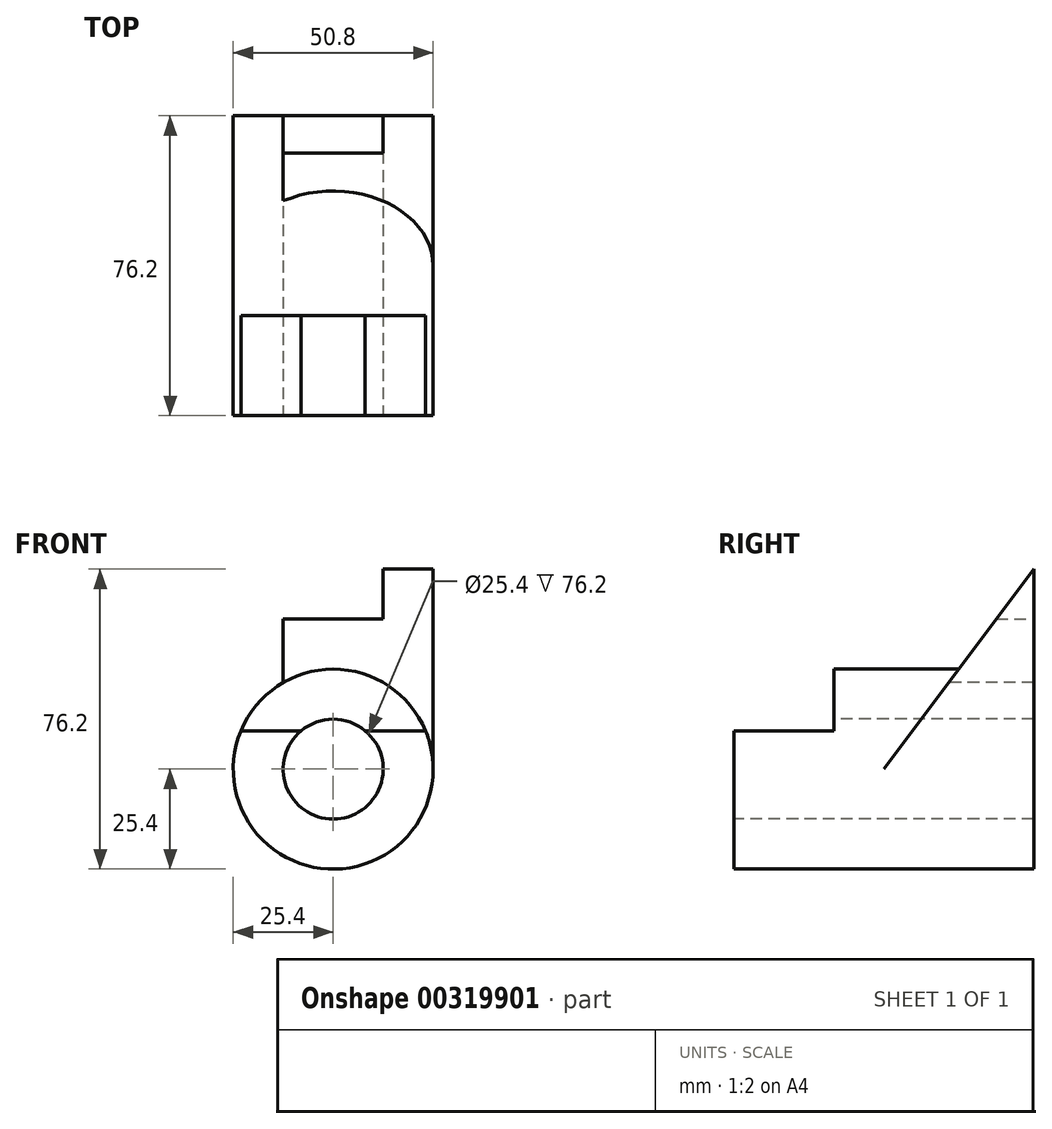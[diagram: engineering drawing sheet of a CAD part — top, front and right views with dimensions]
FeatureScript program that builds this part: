
annotation { "Feature Type Name" : "Feature", "Feature Type Description" : "" }
export const myFeature = defineFeature(function(context is Context, id is Id, definition is map)
    precondition{}
    {
        {
            var Q0;
            Q0=qCreatedBy(makeId("Front.planeOp"),FACE);
            var sketch = newSketch(context, id + "F0", { "sketchPlane" : qUnion([Q0])});
            skCircle(sketch, "E0", {"center": v(0, 0) * mm, "radius": 12.7 * mm});
            skCircle(sketch, "E1", {"center": v(0, 0) * mm, "radius": 25.4 * mm});
            skSolve(sketch);
        }
        {
            var Q0;
            Q0=makeQuery(id+"F0.imprint","IMPRINT",FACE,{"disambiguationData":[TD([[makeQuery(id+"F0.imprint","IMPRINT",EDGE,{"derivedFrom":sQuery(id+"F0.wireOp",EDGE,"E0")}),-1.0]])]});
            extrude(context, id + "F1", {"entities" : qUnion([Q0]), "oppositeDirection" : true, "depth" : 76.2 * mm});
        }
        {
            var Q0;
            Q0=makeQuery(id+"F1.opExtrude","CAP_FACE",FACE,{"disambiguationData":[OSD([sQuery(id+"F0.wireOp",EDGE,"E0"),sQuery(id+"F0.wireOp",EDGE,"E1")])],"isStart":true});
            var sketch = newSketch(context, id + "F2", { "sketchPlane" : qUnion([Q0])});
            skLineSegment(sketch, "E2", {"start": v(0, 25.4) * mm, "end": v(0, 9.53) * mm, "construction": true});
            skLineSegment(sketch, "E3.bottom", {"start": v(25.4, 9.75) * mm, "end": v(-25.4, 9.75) * mm});
            skLineSegment(sketch, "E3.top", {"start": v(25.4, 41.05) * mm, "end": v(-25.4, 41.05) * mm});
            skLineSegment(sketch, "E3.left", {"start": v(25.4, 9.75) * mm, "end": v(25.4, 41.05) * mm});
            skLineSegment(sketch, "E3.right", {"start": v(-25.4, 9.75) * mm, "end": v(-25.4, 41.05) * mm});
            skPoint(sketch, "E3.middle", {"position": v(0, 25.4) * mm});
            skSolve(sketch);
        }
        {
            var Q0;
            {var subQ0=sQuery(id+"F2.wireOp",EDGE,"E3.bottom");var subQ1=makeQuery(id+"F1.opExtrude","CAP_EDGE",EDGE,{"disambiguationData":[OSD([sQuery(id+"F0.wireOp",EDGE,"E1")])],"isStart":true});var subQ2=makeQuery(id+"F2.imprint","INTERSECT",VERTEX,{"disambiguationData":[OD(0.0)],"derivedFrom":[subQ1,subQ0]});Q0=makeQuery(id+"F2.imprint","IMPRINT",FACE,{"disambiguationData":[TD([[makeQuery(id+"F2.imprint","IMPRINT",EDGE,{"disambiguationData":[TD([[subQ2,-1.0]])],"derivedFrom":subQ0}),-1.0]])]});}
            extrude(context, id + "F3", {"entities" : qUnion([Q0]), "operationType" : NewBodyOperationType.REMOVE, "oppositeDirection" : true, "depth" : 12.7 * mm});
        }
        {
            var Q0;
            Q0=makeQuery(id+"F1.opExtrude","CAP_FACE",FACE,{"disambiguationData":[OSD([sQuery(id+"F0.wireOp",EDGE,"E0"),sQuery(id+"F0.wireOp",EDGE,"E1")])],"isStart":true});
            var sketch = newSketch(context, id + "F4", { "sketchPlane" : qUnion([Q0])});
            skPoint(sketch, "E4.endSnap0", {"position": v(0, -12.7) * mm});
            skLineSegment(sketch, "E5", {"start": v(0, 0) * mm, "end": v(0, -9.53) * mm, "construction": true});
            skLineSegment(sketch, "E6", {"start": v(0, -9.53) * mm, "end": v(0, 7.94) * mm, "construction": true});
            skLineSegment(sketch, "E7.bottom", {"start": v(38.1, -9.52) * mm, "end": v(-38.1, -9.53) * mm});
            skLineSegment(sketch, "E7.top", {"start": v(38.1, 25.4) * mm, "end": v(-38.1, 25.4) * mm});
            skLineSegment(sketch, "E7.left", {"start": v(38.1, -9.52) * mm, "end": v(38.1, 25.4) * mm});
            skLineSegment(sketch, "E7.right", {"start": v(-38.1, -9.53) * mm, "end": v(-38.1, 25.4) * mm});
            skPoint(sketch, "E7.middle", {"position": v(0, 7.94) * mm});
            skSolve(sketch);
        }
        {
            var Q0;
            Q0=makeQuery(id+"F4.imprint","IMPRINT",FACE,{"disambiguationData":[TD([[makeQuery(id+"F4.imprint","IMPRINT",EDGE,{"derivedFrom":sQuery(id+"F4.wireOp",EDGE,"E7.top")}),1.0]])]});
            var Q1;
            {var subQ1=makeQuery(id+"F1.opExtrude","CAP_EDGE",EDGE,{"disambiguationData":[OSD([sQuery(id+"F0.wireOp",EDGE,"E1")])],"isStart":true});var subQ7=sQuery(id+"F2.wireOp",EDGE,"E3.bottom");var subQ8=makeQuery(id+"F3.boolean.opBoolean","COPY",EDGE,{"derivedFrom":makeQuery(id+"F3.opExtrude","CAP_EDGE",EDGE,{"disambiguationData":[OSD([subQ7]),TDD([makeQuery(id+"F2.imprint","IMPRINT",EDGE,{"disambiguationData":[TD([[makeQuery(id+"F2.imprint","INTERSECT",VERTEX,{"disambiguationData":[OD(1.0)],"derivedFrom":[subQ1,subQ7]}),1.0]])],"derivedFrom":subQ7})])],"isStart":true})});Q1=makeQuery(id+"F4.imprint","IMPRINT",FACE,{"disambiguationData":[TD([[makeQuery(id+"F4.imprint","IMPRINT",EDGE,{"derivedFrom":subQ8}),1.0]])]});}
            var Q2;
            {var subQ1=makeQuery(id+"F1.opExtrude","CAP_EDGE",EDGE,{"disambiguationData":[OSD([sQuery(id+"F0.wireOp",EDGE,"E1")])],"isStart":true});var subQ7=sQuery(id+"F2.wireOp",EDGE,"E3.bottom");var subQ8=makeQuery(id+"F3.boolean.opBoolean","COPY",EDGE,{"derivedFrom":makeQuery(id+"F3.opExtrude","CAP_EDGE",EDGE,{"disambiguationData":[OSD([subQ7]),TDD([makeQuery(id+"F2.imprint","IMPRINT",EDGE,{"disambiguationData":[TD([[makeQuery(id+"F2.imprint","INTERSECT",VERTEX,{"disambiguationData":[OD(0.0)],"derivedFrom":[subQ1,subQ7]}),-1.0]])],"derivedFrom":subQ7})])],"isStart":true})});Q2=makeQuery(id+"F4.imprint","IMPRINT",FACE,{"disambiguationData":[TD([[makeQuery(id+"F4.imprint","IMPRINT",EDGE,{"derivedFrom":subQ8}),1.0]])]});}
            extrude(context, id + "F5", {"entities" : qUnion([Q0, Q1, Q2]), "operationType" : NewBodyOperationType.REMOVE, "oppositeDirection" : true, "depth" : 25.4 * mm, "hasSecondDirection" : true, "secondDirectionOppositeDirection" : true, "secondDirectionDepth" : 12.7 * mm});
        }
        {
            var Q0;
            Q0=qCreatedBy(makeId("Right.planeOp"),FACE);
            var sketch = newSketch(context, id + "F6", { "sketchPlane" : qUnion([Q0])});
            skLineSegment(sketch, "E8", {"start": v(76.2, 0) * mm, "end": v(38.1, 0) * mm});
            skLineSegment(sketch, "E9", {"start": v(76.2, 0) * mm, "end": v(76.2, 50.8) * mm});
            skLineSegment(sketch, "E10", {"start": v(76.2, 50.8) * mm, "end": v(38.1, 0) * mm});
            skSolve(sketch);
        }
        {
            var Q0;
            Q0 = qSketchRegion(id + "F6", true);
            extrude(context, id + "F7", {"entities" : qUnion([Q0]), "operationType" : NewBodyOperationType.ADD, "depth" : 25.4 * mm, "hasSecondDirection" : true, "secondDirectionOppositeDirection" : true, "secondDirectionDepth" : 12.7 * mm});
        }
        {
            var Q0;
            Q0=makeQuery(id+"F7.boolean.opBoolean","MERGE",FACE,{"derivedFrom":[makeQuery(id+"F1.opExtrude","CAP_FACE",FACE,{"disambiguationData":[OSD([sQuery(id+"F0.wireOp",EDGE,"E0"),sQuery(id+"F0.wireOp",EDGE,"E1")])],"isStart":false}),makeQuery(id+"F7.opExtrude","SWEPT_FACE",FACE,{"disambiguationData":[OSD([sQuery(id+"F6.wireOp",EDGE,"E9")])]})]});
            var sketch = newSketch(context, id + "F8", { "sketchPlane" : qUnion([Q0])});
            skCircle(sketch, "E11", {"center": v(0, 0) * mm, "radius": 12.7 * mm});
            skSolve(sketch);
        }
        {
            var Q0;
            Q0=makeQuery(id+"F8.imprint","IMPRINT",FACE,{"disambiguationData":[TD([[makeQuery(id+"F8.imprint","IMPRINT",EDGE,{"disambiguationData":[OD(0.0)],"derivedFrom":sQuery(id+"F8.wireOp",EDGE,"E11")}),1.0]])]});
            extrude(context, id + "F9", {"entities" : qUnion([Q0]), "operationType" : NewBodyOperationType.REMOVE, "oppositeDirection" : true, "depth" : 38.1 * mm});
        }
        {
            var Q0;
            Q0=makeQuery(id+"F7.boolean.opBoolean","MERGE",FACE,{"derivedFrom":[makeQuery(id+"F1.opExtrude","CAP_FACE",FACE,{"disambiguationData":[OSD([sQuery(id+"F0.wireOp",EDGE,"E0"),sQuery(id+"F0.wireOp",EDGE,"E1")])],"isStart":false}),makeQuery(id+"F7.opExtrude","SWEPT_FACE",FACE,{"disambiguationData":[OSD([sQuery(id+"F6.wireOp",EDGE,"E9")])]})]});
            var sketch = newSketch(context, id + "F10", { "sketchPlane" : qUnion([Q0])});
            skLineSegment(sketch, "E12", {"start": v(-12.7, 50.8) * mm, "end": v(-12.7, 38.1) * mm});
            skLineSegment(sketch, "E13", {"start": v(-12.7, 38.1) * mm, "end": v(12.7, 38.1) * mm});
            skLineSegment(sketch, "E14", {"start": v(12.7, 38.1) * mm, "end": v(12.7, 50.8) * mm});
            skLineSegment(sketch, "E15", {"start": v(12.7, 50.8) * mm, "end": v(-12.7, 50.8) * mm});
            skSolve(sketch);
        }
        {
            var Q0;
            Q0=makeQuery(id+"F10.imprint","IMPRINT",FACE,{"disambiguationData":[TD([[makeQuery(id+"F10.imprint","IMPRINT",EDGE,{"derivedFrom":sQuery(id+"F10.wireOp",EDGE,"E12")}),1.0]])]});
            extrude(context, id + "F11", {"entities" : qUnion([Q0]), "operationType" : NewBodyOperationType.REMOVE, "oppositeDirection" : true, "depth" : 25.4 * mm});
        }
    });
